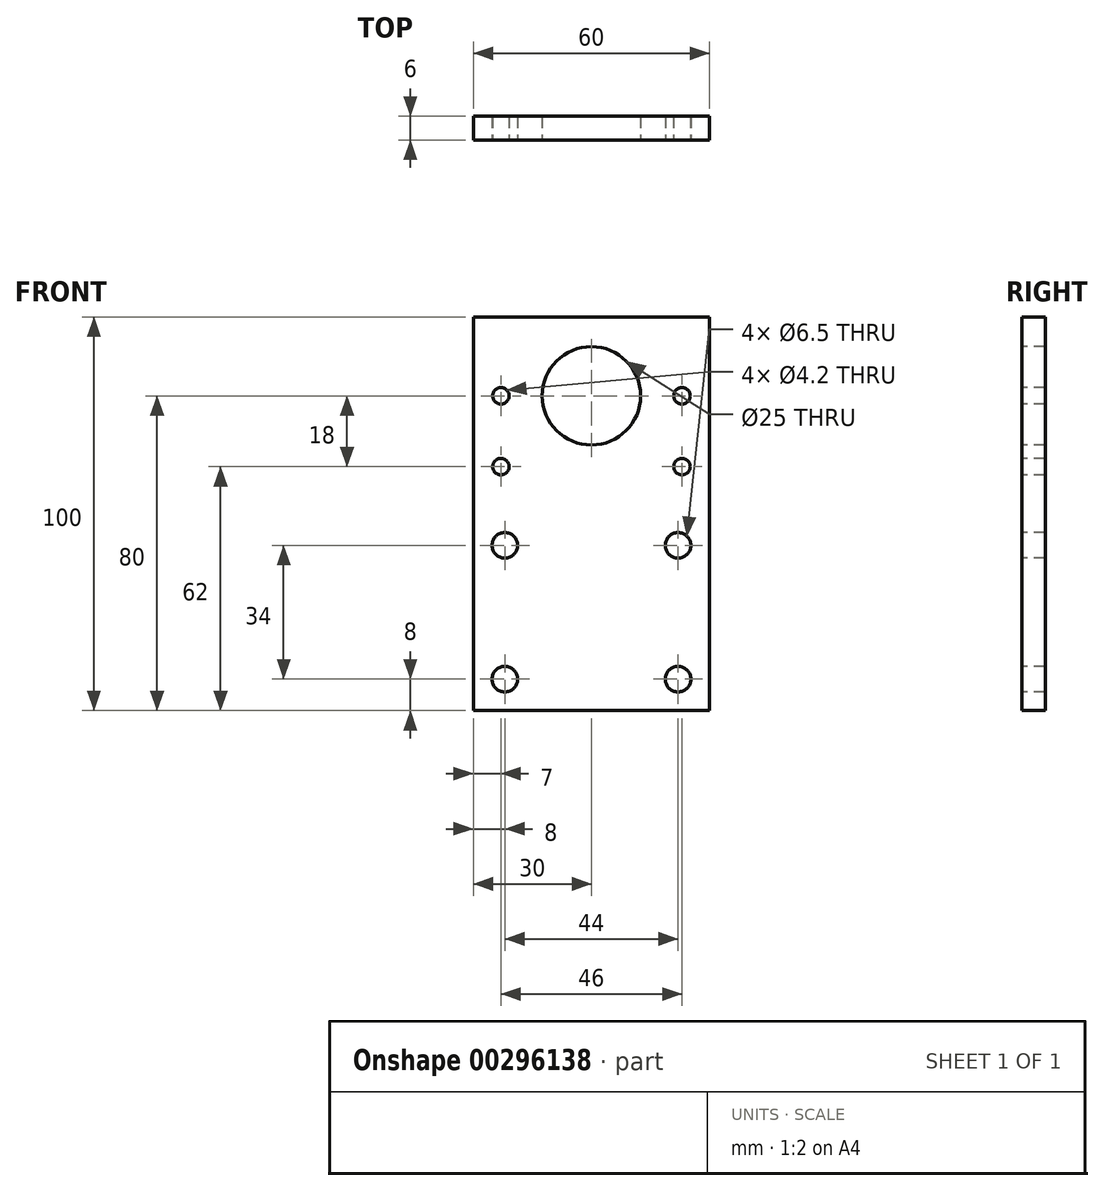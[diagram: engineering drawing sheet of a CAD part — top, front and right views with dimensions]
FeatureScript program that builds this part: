
annotation { "Feature Type Name" : "Feature", "Feature Type Description" : "" }
export const myFeature = defineFeature(function(context is Context, id is Id, definition is map)
    precondition{}
    {
        {
            var Q0;
            Q0=qCreatedBy(makeId("Front.planeOp"),FACE);
            var sketch = newSketch(context, id + "F0", { "sketchPlane" : qUnion([Q0])});
            skLineSegment(sketch, "E0.bottom", {"start": v(30, 50) * mm, "end": v(-30, 50) * mm});
            skLineSegment(sketch, "E0.top", {"start": v(30, -50) * mm, "end": v(-30, -50) * mm});
            skLineSegment(sketch, "E0.left", {"start": v(30, 50) * mm, "end": v(30, -50) * mm});
            skLineSegment(sketch, "E0.right", {"start": v(-30, 50) * mm, "end": v(-30, -50) * mm});
            skPoint(sketch, "E0.middle", {"position": v(0, 0) * mm});
            skCircle(sketch, "E1", {"center": v(0, 30) * mm, "radius": 12.5 * mm});
            skLineSegment(sketch, "E2", {"start": v(-23, 30) * mm, "end": v(23, 30) * mm, "construction": true});
            skCircle(sketch, "E3", {"center": v(-23, 30) * mm, "radius": 2.1 * mm});
            skCircle(sketch, "E4", {"center": v(23, 30) * mm, "radius": 2.1 * mm});
            skLineSegment(sketch, "E5", {"start": v(0, -12.6) * mm, "end": v(0, 30.4) * mm, "construction": true});
            skCircle(sketch, "E6", {"center": v(-23, 12) * mm, "radius": 2.1 * mm});
            skCircle(sketch, "E7", {"center": v(23, 12) * mm, "radius": 2.1 * mm});
            skLineSegment(sketch, "E8.bottom", {"start": v(-22, -8) * mm, "end": v(22, -8) * mm, "construction": true});
            skLineSegment(sketch, "E8.top", {"start": v(-22, -42) * mm, "end": v(22, -42) * mm, "construction": true});
            skLineSegment(sketch, "E8.left", {"start": v(-22, -8) * mm, "end": v(-22, -42) * mm, "construction": true});
            skLineSegment(sketch, "E8.right", {"start": v(22, -8) * mm, "end": v(22, -42) * mm, "construction": true});
            skPoint(sketch, "E8.middle", {"position": v(0, -25) * mm});
            skCircle(sketch, "E9", {"center": v(-22, -8) * mm, "radius": 3.25 * mm});
            skCircle(sketch, "E10", {"center": v(22, -8) * mm, "radius": 3.25 * mm});
            skCircle(sketch, "E11", {"center": v(22, -42) * mm, "radius": 3.25 * mm});
            skCircle(sketch, "E12", {"center": v(-22, -42) * mm, "radius": 3.25 * mm});
            skSolve(sketch);
        }
        {
            var Q0;
            Q0=makeQuery(id+"F0.imprint","IMPRINT",FACE,{"disambiguationData":[TD([[makeQuery(id+"F0.imprint","IMPRINT",EDGE,{"derivedFrom":sQuery(id+"F0.wireOp",EDGE,"E0.bottom")}),1.0]])]});
            extrude(context, id + "F1", {"entities" : qUnion([Q0]), "oppositeDirection" : true, "depth" : 6 * mm, "offsetDistance" : 25 * mm});
        }
    });
